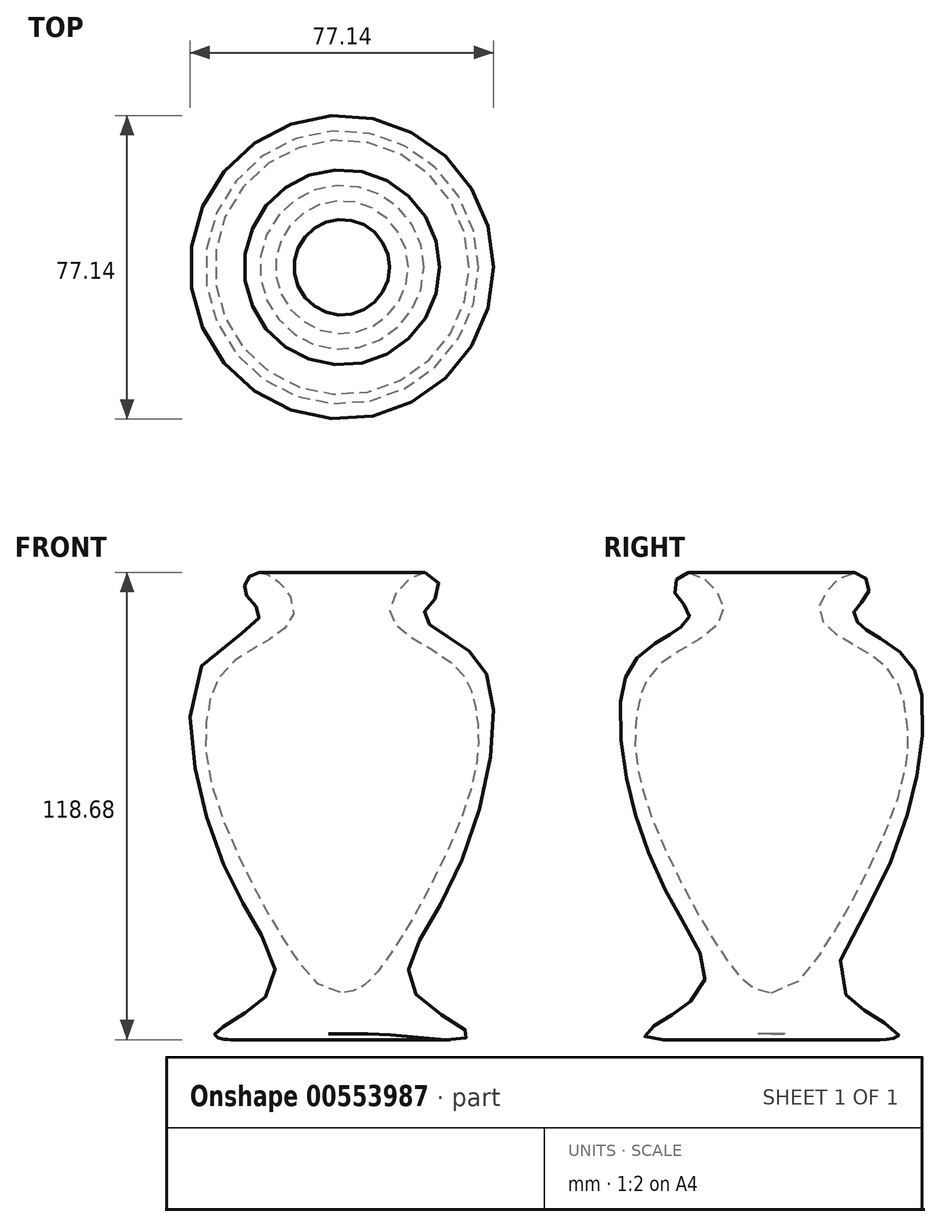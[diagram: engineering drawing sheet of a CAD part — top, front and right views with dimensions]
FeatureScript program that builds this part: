
annotation { "Feature Type Name" : "Feature", "Feature Type Description" : "" }
export const myFeature = defineFeature(function(context is Context, id is Id, definition is map)
    precondition{}
    {
        {
            var Q0;
            Q0=qCreatedBy(makeId("Front.planeOp"),FACE);
            var sketch = newSketch(context, id + "F0", { "sketchPlane" : qUnion([Q0])});
            skFitSpline(sketch, "E0", {"points": [v(1.17, 0) * mm, v(12.84, -0.33) * mm, v(29.87, -1.39) * mm, v(32.26, 0) * mm, v(17.88, 11.37) * mm, v(27.67, 37.8) * mm, v(36.9, 91.01) * mm, v(24.8, 102.15) * mm, v(20.9, 107.07) * mm, v(24.71, 112.47) * mm, v(21.14, 117.18) * mm, v(12.17, 107.04) * mm, v(27.8, 94.36) * mm, v(34.13, 81.6) * mm, v(31.9, 59.15) * mm, v(6.68, 13.13) * mm, v(0, 10.4) * mm], "startDerivative": vector(232.35, 0) * mm, "endDerivative": vector(-177.8, -30.88) * mm});
            skLineSegment(sketch, "E1", {"start": v(1.17, 0) * mm, "end": v(0, 0) * mm});
            skLineSegment(sketch, "E2", {"start": v(0, 0) * mm, "end": v(0, 10.4) * mm});
            skLineSegment(sketch, "E3", {"start": v(0, 0) * mm, "end": v(0, 75.48) * mm});
            skSolve(sketch);
        }
        {
            var Q0;
            {var subQ0=sQuery(id+"F0.wireOp",EDGE,"E0");Q0=makeQuery(id+"F0.imprint","IMPRINT",FACE,{"disambiguationData":[TD([[makeQuery(id+"F0.imprint","IMPRINT",EDGE,{"derivedFrom":subQ0}),1.0]])]});}
            var Q1;
            Q1=sQuery(id+"F0.wireOp",EDGE,"E3");
            revolve(context, id + "F1", {"entities" : qUnion([Q0]), "axis" : qUnion([Q1]), "revolveType" : RevolveType.FULL});
        }
    });
